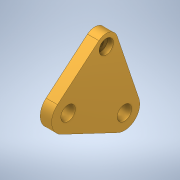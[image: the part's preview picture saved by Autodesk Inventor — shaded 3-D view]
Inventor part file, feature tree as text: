
AUTODESK INVENTOR PART (.ipt)
format: ipt  version: 2020 (Build 240168000, 168)  size: 152,064 bytes
history: native  units: in
note: dims shown in document units (in); Inventor stores cm internally (conversion verified against a paired STEP export)
features: extrude x3, sketch x3, projected_geometry x1
ambient origin geometry x8: Origin, YZ Plane, XZ Plane, XY Plane, X Axis, Y Axis, Z Axis, Center Point
bodies: Solid1 (feature_tree)
feature tree (7):
  extrude  "Extrusion1"  Depth=0.4523in
  extrude  "Extrusion2"  Depth=0.2118in
  extrude  "Extrusion3"  Depth=0.1575in TaperAngle=0.0deg
  sketch  "Sketch1"  dims[d0=0.2008in d1=0.2008in d3=0.4523in]
  sketch  "Sketch2"  dims[d4=0.2118in d5=0.8586in]
  projected_geometry  "Projected Loop1"
  sketch  "Sketch3"  dims[d6=0.8656in d7=0.1575in d8=0.0in d11=0.0787in d12=0.315in d13=0.1575in d14=0.0in d15=0.1969in d16=0.0787in d17=0.0in d20=0.7087in d21=0.4622in]
